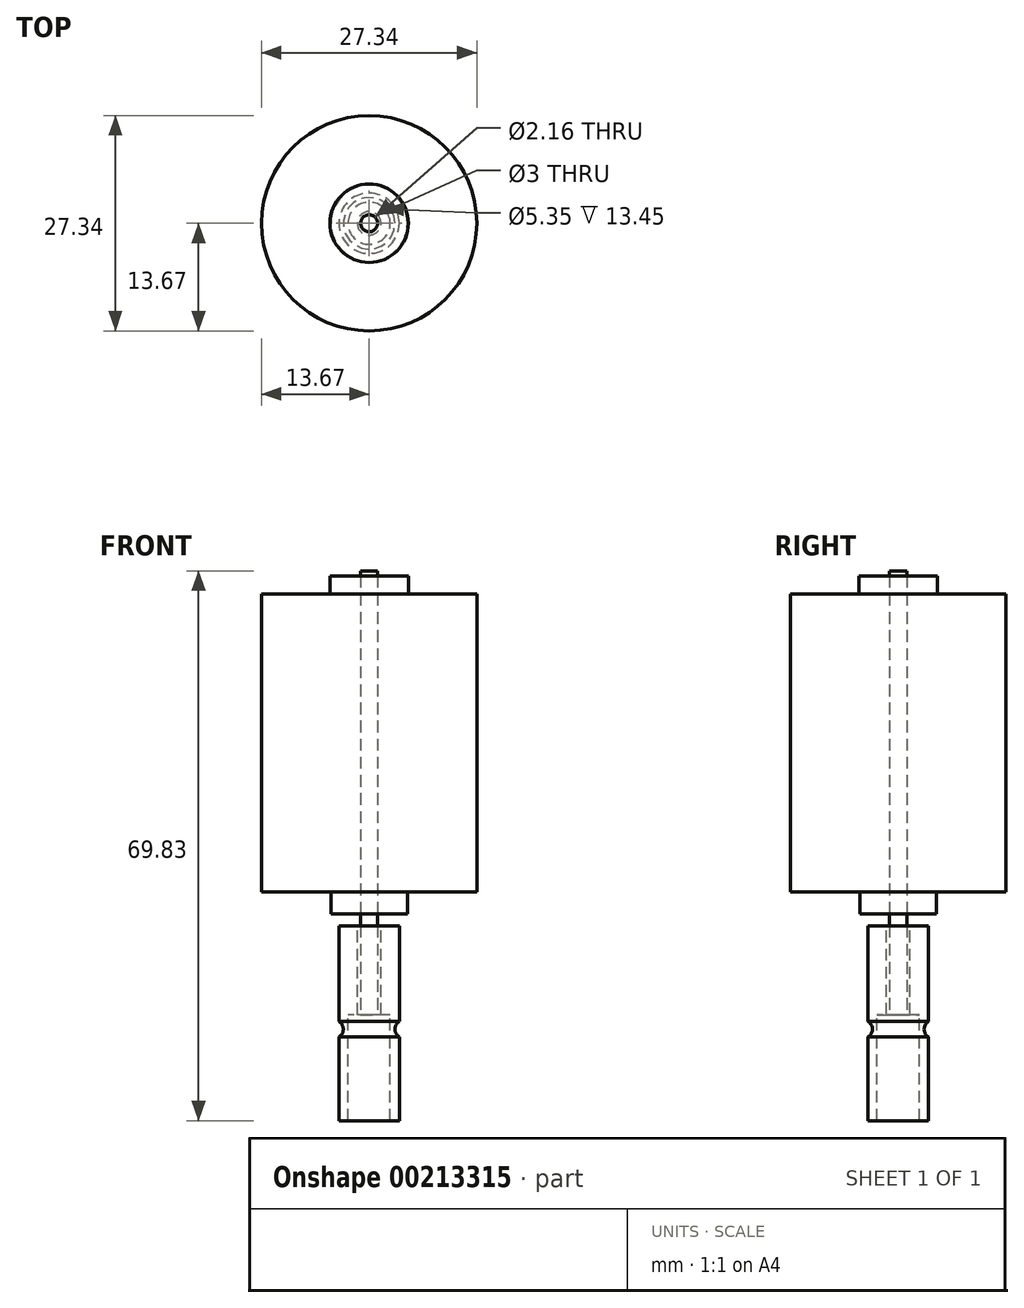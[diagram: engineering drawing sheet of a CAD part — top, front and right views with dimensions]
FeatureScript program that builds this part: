
annotation { "Feature Type Name" : "Feature", "Feature Type Description" : "" }
export const myFeature = defineFeature(function(context is Context, id is Id, definition is map)
    precondition{}
    {
        {
            var Q0;
            Q0=qCreatedBy(makeId("Front.planeOp"),FACE);
            var sketch = newSketch(context, id + "F0", { "sketchPlane" : qUnion([Q0])});
            skLineSegment(sketch, "E0", {"start": v(0, 0) * mm, "end": v(0, 40.76) * mm});
            skLineSegment(sketch, "E1", {"start": v(0, 0) * mm, "end": v(0, -15.62) * mm});
            skLineSegment(sketch, "E2", {"start": v(1.08, -2.8) * mm, "end": v(4.86, -2.8) * mm});
            skLineSegment(sketch, "E3", {"start": v(4.86, -2.8) * mm, "end": v(4.86, 0) * mm});
            skLineSegment(sketch, "E4", {"start": v(4.86, 0) * mm, "end": v(13.67, 0) * mm});
            skLineSegment(sketch, "E5", {"start": v(13.67, 0) * mm, "end": v(13.67, 37.84) * mm});
            skLineSegment(sketch, "E6", {"start": v(13.67, 37.84) * mm, "end": v(4.98, 37.84) * mm});
            skLineSegment(sketch, "E7", {"start": v(4.98, 37.84) * mm, "end": v(4.98, 40.14) * mm});
            skLineSegment(sketch, "E8", {"start": v(4.98, 40.14) * mm, "end": v(1.08, 40.14) * mm});
            skLineSegment(sketch, "E9", {"start": v(0, 40.76) * mm, "end": v(1.08, 40.76) * mm});
            skLineSegment(sketch, "E10", {"start": v(1.08, -15.62) * mm, "end": v(0, -15.62) * mm});
            skLineSegment(sketch, "E11", {"start": v(1.08, 40.76) * mm, "end": v(1.08, -15.62) * mm});
            skLineSegment(sketch, "E12", {"start": v(1.5, -4.3) * mm, "end": v(3.84, -4.3) * mm});
            skLineSegment(sketch, "E13", {"start": v(3.84, -4.3) * mm, "end": v(3.84, -16.48) * mm});
            skArc(sketch, "E14", {"start": v(3.84, -16.48) * mm, "mid": v(3.28, -17.45) * mm, "end": v(3.84, -18.42) * mm});
            skLineSegment(sketch, "E15", {"start": v(3.84, -18.42) * mm, "end": v(3.84, -29.07) * mm});
            skLineSegment(sketch, "E16", {"start": v(3.84, -29.07) * mm, "end": v(2.68, -29.07) * mm});
            skLineSegment(sketch, "E17", {"start": v(2.68, -29.07) * mm, "end": v(2.67, -15.62) * mm});
            skLineSegment(sketch, "E18", {"start": v(2.67, -15.62) * mm, "end": v(1.5, -15.62) * mm});
            skLineSegment(sketch, "E19", {"start": v(1.5, -15.62) * mm, "end": v(1.5, -4.3) * mm});
            skSolve(sketch);
        }
        {
            var Q0;
            Q0=makeQuery(id+"F0.imprint","IMPRINT",FACE,{"disambiguationData":[TD([[makeQuery(id+"F0.imprint","IMPRINT",EDGE,{"derivedFrom":sQuery(id+"F0.wireOp",EDGE,"E0")}),-1.0]])]});
            var Q1;
            Q1=sQuery(id+"F0.wireOp",EDGE,"E0");
            revolve(context, id + "F1", {"entities" : qUnion([Q0]), "axis" : qUnion([Q1]), "revolveType" : RevolveType.FULL});
        }
        {
            var Q0;
            {var subQ1=sQuery(id+"F0.wireOp",EDGE,"E2");Q0=makeQuery(id+"F0.imprint","IMPRINT",FACE,{"disambiguationData":[TD([[makeQuery(id+"F0.imprint","IMPRINT",EDGE,{"derivedFrom":subQ1}),1.0]])]});}
            var Q1;
            Q1=sQuery(id+"F0.wireOp",EDGE,"E0");
            revolve(context, id + "F2", {"entities" : qUnion([Q0]), "axis" : qUnion([Q1]), "revolveType" : RevolveType.FULL});
        }
        {
            var Q0;
            Q0=makeQuery(id+"F0.imprint","IMPRINT",FACE,{"disambiguationData":[TD([[makeQuery(id+"F0.imprint","IMPRINT",EDGE,{"derivedFrom":sQuery(id+"F0.wireOp",EDGE,"E12")}),-1.0]])]});
            var Q1;
            Q1=sQuery(id+"F0.wireOp",EDGE,"E1");
            revolve(context, id + "F3", {"entities" : qUnion([Q0]), "axis" : qUnion([Q1]), "revolveType" : RevolveType.FULL});
        }
    });
